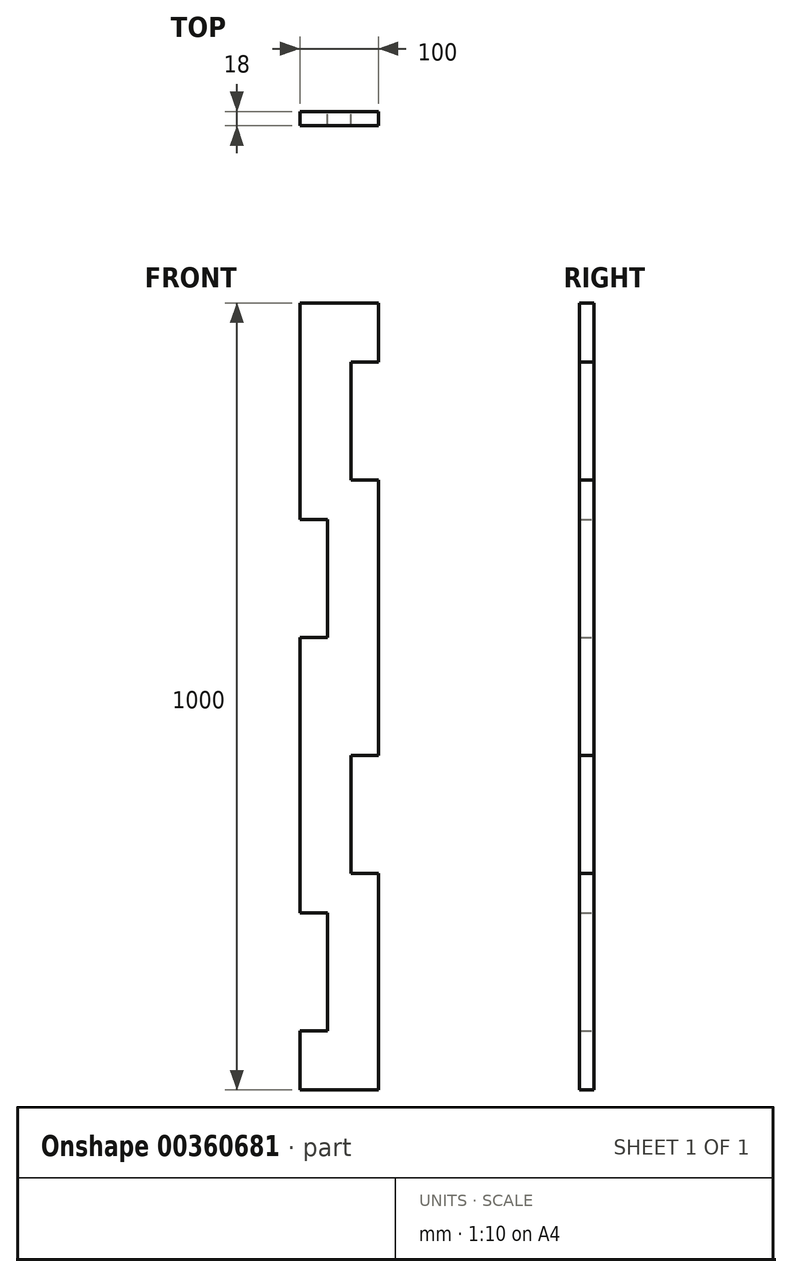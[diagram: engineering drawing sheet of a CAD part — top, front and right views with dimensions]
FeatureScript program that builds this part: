
annotation { "Feature Type Name" : "Feature", "Feature Type Description" : "" }
export const myFeature = defineFeature(function(context is Context, id is Id, definition is map)
    precondition{}
    {
        {
            var Q0;
            Q0=qCreatedBy(makeId("Front.planeOp"),FACE);
            var sketch = newSketch(context, id + "F0", { "sketchPlane" : qUnion([Q0])});
            skLineSegment(sketch, "E0.bottom", {"start": v(-50, 0) * mm, "end": v(50, 0) * mm});
            skLineSegment(sketch, "E0.top", {"start": v(-50, 1000) * mm, "end": v(50, 1000) * mm});
            skLineSegment(sketch, "E0.right", {"start": v(50, 0) * mm, "end": v(50, 275) * mm});
            skLineSegment(sketch, "E1.bottom", {"start": v(50, 925) * mm, "end": v(15, 925) * mm});
            skLineSegment(sketch, "E1.top", {"start": v(50, 775) * mm, "end": v(15, 775) * mm});
            skLineSegment(sketch, "E1.right", {"start": v(15, 925) * mm, "end": v(15, 775) * mm});
            skLineSegment(sketch, "E2.bottom", {"start": v(50, 425) * mm, "end": v(15, 425) * mm});
            skLineSegment(sketch, "E2.top", {"start": v(50, 275) * mm, "end": v(15, 275) * mm});
            skLineSegment(sketch, "E2.right", {"start": v(15, 425) * mm, "end": v(15, 275) * mm});
            skLineSegment(sketch, "E3.trimOffspring", {"start": v(50, 925) * mm, "end": v(50, 1000) * mm});
            skLineSegment(sketch, "E4.trimOffspring", {"start": v(50, 425) * mm, "end": v(50, 775) * mm});
            skLineSegment(sketch, "E5", {"start": v(-50, 1000) * mm, "end": v(-50, 725) * mm});
            skPoint(sketch, "E0.left.start.orphan", {"position": v(0, 0) * mm});
            skLineSegment(sketch, "E6.bottom", {"start": v(-50, 225) * mm, "end": v(-15, 225) * mm});
            skLineSegment(sketch, "E6.top", {"start": v(-50, 75) * mm, "end": v(-15, 75) * mm});
            skLineSegment(sketch, "E6.right", {"start": v(-15, 225) * mm, "end": v(-15, 75) * mm});
            skLineSegment(sketch, "E7.bottom", {"start": v(-50, 725) * mm, "end": v(-15, 725) * mm});
            skLineSegment(sketch, "E7.top", {"start": v(-50, 575) * mm, "end": v(-15, 575) * mm});
            skLineSegment(sketch, "E7.right", {"start": v(-15, 725) * mm, "end": v(-15, 575) * mm});
            skLineSegment(sketch, "E8.trimOffspring", {"start": v(-50, 575) * mm, "end": v(-50, 225) * mm});
            skLineSegment(sketch, "E9.trimOffspring", {"start": v(-50, 75) * mm, "end": v(-50, 0) * mm});
            skSolve(sketch);
        }
        {
            var Q0;
            Q0=makeQuery(id+"F0.imprint","IMPRINT",FACE,{"disambiguationData":[TD([[makeQuery(id+"F0.imprint","IMPRINT",EDGE,{"derivedFrom":sQuery(id+"F0.wireOp",EDGE,"E0.bottom")}),1.0]])]});
            extrude(context, id + "F1", {"entities" : qUnion([Q0]), "depth" : 18 * mm});
        }
    });
